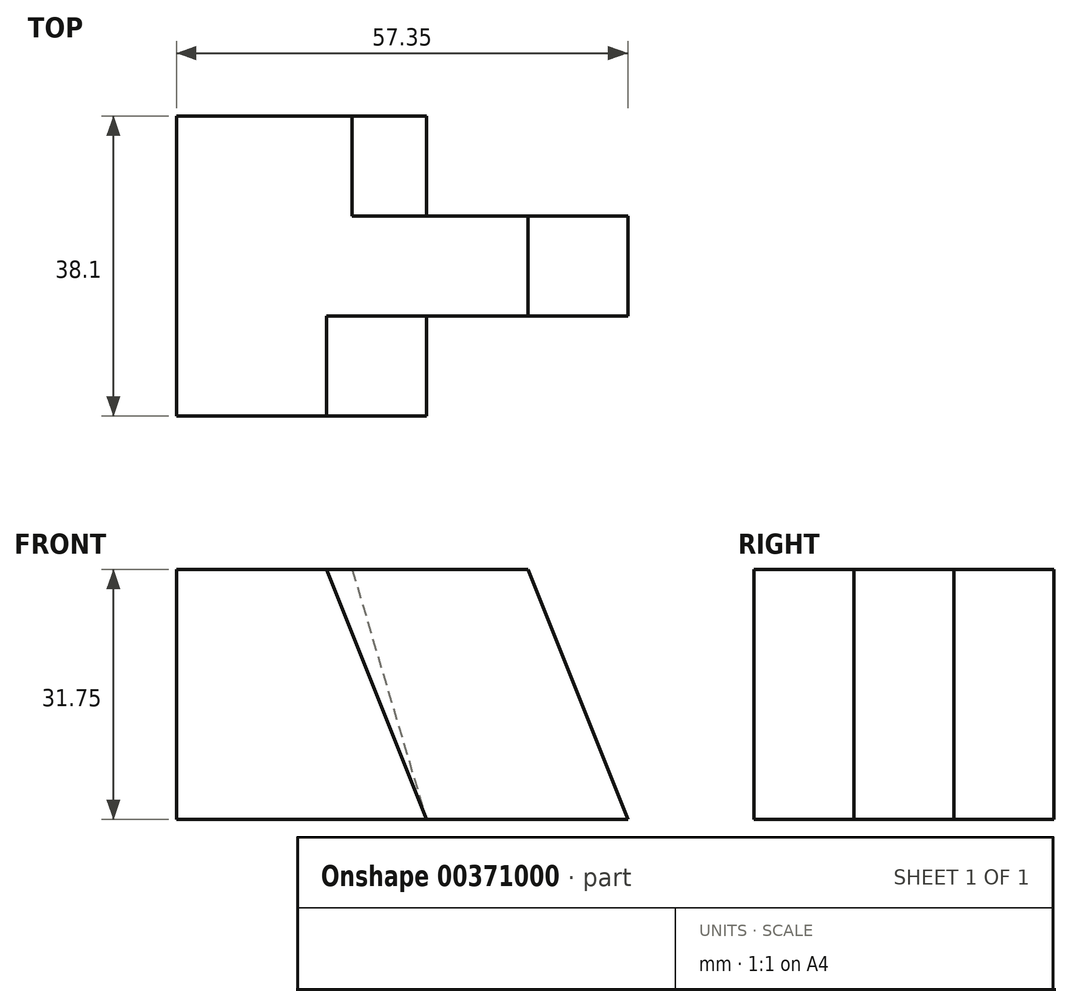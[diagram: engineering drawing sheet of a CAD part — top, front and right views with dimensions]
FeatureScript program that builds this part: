
annotation { "Feature Type Name" : "Feature", "Feature Type Description" : "" }
export const myFeature = defineFeature(function(context is Context, id is Id, definition is map)
    precondition{}
    {
        {
            var Q0;
            Q0=qCreatedBy(makeId("Front.planeOp"),FACE);
            var sketch = newSketch(context, id + "F0", { "sketchPlane" : qUnion([Q0])});
            skLineSegment(sketch, "E0", {"start": v(-53.53, 0) * mm, "end": v(-53.53, 31.75) * mm});
            skLineSegment(sketch, "E1", {"start": v(-53.53, 31.75) * mm, "end": v(-9.08, 31.75) * mm});
            skLineSegment(sketch, "E2", {"start": v(-53.53, 0) * mm, "end": v(3.62, 0) * mm});
            skLineSegment(sketch, "E3", {"start": v(-9.08, 31.75) * mm, "end": v(3.62, 0) * mm});
            skSolve(sketch);
        }
        {
            var Q0;
            Q0 = qSketchRegion(id + "F0", true);
            extrude(context, id + "F1", {"entities" : qUnion([Q0]), "depth" : 12.7 * mm});
        }
        {
            var Q0;
            Q0=qCreatedBy(makeId("Front.planeOp"),FACE);
            var sketch = newSketch(context, id + "F2", { "sketchPlane" : qUnion([Q0])});
            skLineSegment(sketch, "E4", {"start": v(-53.73, 0) * mm, "end": v(-53.73, 31.75) * mm});
            skLineSegment(sketch, "E5", {"start": v(-53.73, 31.75) * mm, "end": v(-34.68, 31.75) * mm});
            skLineSegment(sketch, "E6", {"start": v(-53.73, 0) * mm, "end": v(-21.98, 0) * mm});
            skLineSegment(sketch, "E7", {"start": v(-34.68, 31.75) * mm, "end": v(-21.98, 0) * mm});
            skSolve(sketch);
        }
        {
            var Q0;
            Q0=makeQuery(id+"F2.imprint","IMPRINT",FACE,{"disambiguationData":[TD([[makeQuery(id+"F2.imprint","IMPRINT",EDGE,{"derivedFrom":sQuery(id+"F2.wireOp",EDGE,"E4")}),-1.0]])]});
            extrude(context, id + "F3", {"entities" : qUnion([Q0]), "operationType" : NewBodyOperationType.ADD, "depth" : 12.7 * mm});
        }
        {
            var Q0;
            Q0=qCreatedBy(makeId("Front.planeOp"),FACE);
            var sketch = newSketch(context, id + "F4", { "sketchPlane" : qUnion([Q0])});
            skLineSegment(sketch, "E8", {"start": v(-53.73, 0) * mm, "end": v(-53.73, 31.75) * mm});
            skLineSegment(sketch, "E9", {"start": v(-53.73, 31.75) * mm, "end": v(-34.68, 31.75) * mm});
            skLineSegment(sketch, "E10", {"start": v(-53.73, 0) * mm, "end": v(-21.98, 0) * mm});
            skLineSegment(sketch, "E11", {"start": v(-34.68, 31.75) * mm, "end": v(-21.98, 0) * mm});
            skSolve(sketch);
        }
        {
            var Q0;
            Q0=makeQuery(id+"F4.imprint","IMPRINT",FACE,{"disambiguationData":[TD([[makeQuery(id+"F4.imprint","IMPRINT",EDGE,{"derivedFrom":sQuery(id+"F4.wireOp",EDGE,"E8")}),-1.0]])]});
            extrude(context, id + "F5", {"entities" : qUnion([Q0]), "operationType" : NewBodyOperationType.ADD, "depth" : 25.4 * mm});
        }
        {
            var Q0;
            Q0=makeQuery(id+"F3.boolean.opBoolean","MERGE",FACE,{"derivedFrom":[makeQuery(id+"F1.opExtrude","CAP_FACE",FACE,{"disambiguationData":[OSD([sQuery(id+"F0.wireOp",EDGE,"E0"),sQuery(id+"F0.wireOp",EDGE,"E1"),sQuery(id+"F0.wireOp",EDGE,"E2"),sQuery(id+"F0.wireOp",EDGE,"E3")])],"isStart":true}),makeQuery(id+"F3.opExtrude","CAP_FACE",FACE,{"disambiguationData":[OSD([sQuery(id+"F2.wireOp",EDGE,"E4"),sQuery(id+"F2.wireOp",EDGE,"E5"),sQuery(id+"F2.wireOp",EDGE,"E6"),sQuery(id+"F2.wireOp",EDGE,"E7")])],"isStart":true})]});
            var sketch = newSketch(context, id + "F6", { "sketchPlane" : qUnion([Q0])});
            skLineSegment(sketch, "E12", {"start": v(53.73, 0) * mm, "end": v(53.73, 31.75) * mm});
            skLineSegment(sketch, "E13", {"start": v(53.73, 31.75) * mm, "end": v(31.4, 31.75) * mm});
            skLineSegment(sketch, "E14", {"start": v(53.73, 0) * mm, "end": v(21.98, 0) * mm});
            skLineSegment(sketch, "E15", {"start": v(31.4, 31.75) * mm, "end": v(21.98, 0) * mm});
            skSolve(sketch);
        }
        {
            var Q0;
            Q0=makeQuery(id+"F6.imprint","IMPRINT",FACE,{"disambiguationData":[TD([[makeQuery(id+"F6.imprint","IMPRINT",EDGE,{"derivedFrom":sQuery(id+"F6.wireOp",EDGE,"E12")}),1.0]])]});
            extrude(context, id + "F7", {"entities" : qUnion([Q0]), "operationType" : NewBodyOperationType.ADD, "depth" : 12.7 * mm});
        }
    });
